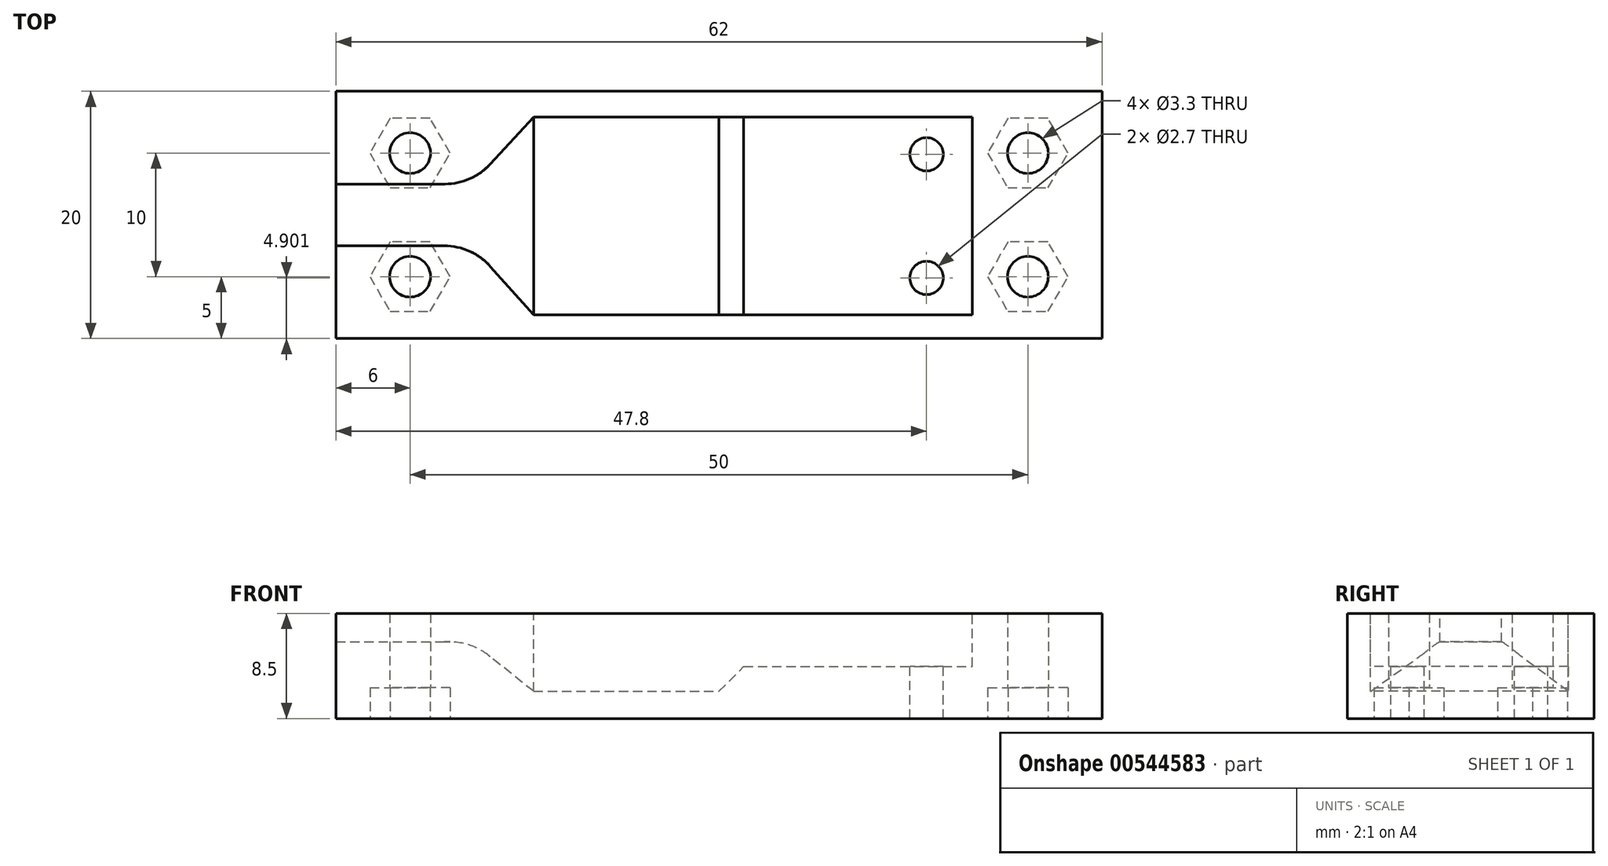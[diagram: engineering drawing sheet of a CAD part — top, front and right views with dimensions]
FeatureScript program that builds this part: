
annotation { "Feature Type Name" : "Feature", "Feature Type Description" : "" }
export const myFeature = defineFeature(function(context is Context, id is Id, definition is map)
    precondition{}
    {
        {
            var Q0;
            Q0=qCreatedBy(makeId("Top.planeOp"),FACE);
            var sketch = newSketch(context, id + "F0", { "sketchPlane" : qUnion([Q0])});
            skLineSegment(sketch, "E0.bottom", {"start": v(0, 0) * mm, "end": v(65, 0) * mm});
            skLineSegment(sketch, "E0.top", {"start": v(0, 20) * mm, "end": v(65, 20) * mm});
            skLineSegment(sketch, "E0.left", {"start": v(0, 0) * mm, "end": v(0, 20) * mm});
            skLineSegment(sketch, "E0.right", {"start": v(65, 0) * mm, "end": v(65, 20) * mm});
            skSolve(sketch);
        }
        {
            var Q0;
            Q0 = qSketchRegion(id + "F0", true);
            extrude(context, id + "F1", {"entities" : qUnion([Q0]), "depth" : 7.5 * mm, "offsetDistance" : 25 * mm});
        }
        {
            var Q0;
            Q0=makeQuery(id+"F1.opExtrude","CAP_FACE",FACE,{"disambiguationData":[OSD([sQuery(id+"F0.wireOp",EDGE,"E0.bottom"),sQuery(id+"F0.wireOp",EDGE,"E0.top"),sQuery(id+"F0.wireOp",EDGE,"E0.left"),sQuery(id+"F0.wireOp",EDGE,"E0.right")])],"isStart":true});
            var sketch = newSketch(context, id + "F2", { "sketchPlane" : qUnion([Q0])});
            skCircle(sketch, "E1.cCircle", {"center": v(6, -5) * mm, "radius": 2.81 * mm, "construction": true});
            skLineSegment(sketch, "E1.0", {"start": v(7.63, -7.81) * mm, "end": v(4.38, -7.81) * mm});
            skLineSegment(sketch, "E1.1", {"start": v(4.38, -7.81) * mm, "end": v(2.75, -5) * mm});
            skLineSegment(sketch, "E1.2", {"start": v(2.75, -5) * mm, "end": v(4.37, -2.19) * mm});
            skLineSegment(sketch, "E1.3", {"start": v(4.37, -2.19) * mm, "end": v(7.63, -2.19) * mm});
            skLineSegment(sketch, "E1.4", {"start": v(7.63, -2.19) * mm, "end": v(9.25, -5) * mm});
            skLineSegment(sketch, "E1.5", {"start": v(9.25, -5) * mm, "end": v(7.63, -7.81) * mm});
            skPoint(sketch, "E1.0.midPoint", {"position": v(6, -7.81) * mm});
            skCircle(sketch, "E2.cCircle", {"center": v(6, -15) * mm, "radius": 2.81 * mm, "construction": true});
            skLineSegment(sketch, "E2.0", {"start": v(4.38, -12.19) * mm, "end": v(7.63, -12.19) * mm});
            skLineSegment(sketch, "E2.1", {"start": v(7.63, -12.19) * mm, "end": v(9.25, -15) * mm});
            skLineSegment(sketch, "E2.2", {"start": v(9.25, -15) * mm, "end": v(7.63, -17.81) * mm});
            skLineSegment(sketch, "E2.3", {"start": v(7.62, -17.81) * mm, "end": v(4.38, -17.81) * mm});
            skLineSegment(sketch, "E2.4", {"start": v(4.38, -17.81) * mm, "end": v(2.75, -15) * mm});
            skLineSegment(sketch, "E2.5", {"start": v(2.75, -15) * mm, "end": v(4.38, -12.19) * mm});
            skPoint(sketch, "E2.0.midPoint", {"position": v(6, -12.19) * mm});
            skCircle(sketch, "E3.cCircle", {"center": v(56, -5) * mm, "radius": 2.81 * mm, "construction": true});
            skLineSegment(sketch, "E3.0", {"start": v(57.62, -7.81) * mm, "end": v(54.38, -7.81) * mm});
            skLineSegment(sketch, "E3.1", {"start": v(54.38, -7.81) * mm, "end": v(52.75, -5) * mm});
            skLineSegment(sketch, "E3.2", {"start": v(52.75, -5) * mm, "end": v(54.38, -2.19) * mm});
            skLineSegment(sketch, "E3.3", {"start": v(54.38, -2.19) * mm, "end": v(57.63, -2.19) * mm});
            skLineSegment(sketch, "E3.4", {"start": v(57.63, -2.19) * mm, "end": v(59.25, -5) * mm});
            skLineSegment(sketch, "E3.5", {"start": v(59.25, -5) * mm, "end": v(57.63, -7.81) * mm});
            skPoint(sketch, "E3.0.midPoint", {"position": v(56, -7.81) * mm});
            skCircle(sketch, "E4.cCircle", {"center": v(56, -15) * mm, "radius": 2.81 * mm, "construction": true});
            skLineSegment(sketch, "E4.0", {"start": v(57.62, -17.81) * mm, "end": v(54.37, -17.81) * mm});
            skLineSegment(sketch, "E4.1", {"start": v(54.37, -17.81) * mm, "end": v(52.75, -15) * mm});
            skLineSegment(sketch, "E4.2", {"start": v(52.75, -15) * mm, "end": v(54.38, -12.19) * mm});
            skLineSegment(sketch, "E4.3", {"start": v(54.38, -12.19) * mm, "end": v(57.63, -12.19) * mm});
            skLineSegment(sketch, "E4.4", {"start": v(57.63, -12.19) * mm, "end": v(59.25, -15) * mm});
            skLineSegment(sketch, "E4.5", {"start": v(59.25, -15) * mm, "end": v(57.62, -17.81) * mm});
            skPoint(sketch, "E4.0.midPoint", {"position": v(56, -17.81) * mm});
            skSolve(sketch);
        }
        {
            var Q0;
            Q0 = qSketchRegion(id + "F2", true);
            extrude(context, id + "F3", {"entities" : qUnion([Q0]), "operationType" : NewBodyOperationType.REMOVE, "oppositeDirection" : true, "depth" : 2.5 * mm, "offsetDistance" : 25 * mm});
        }
        {
            var Q0;
            Q0=makeQuery(id+"F3.boolean.opBoolean","COPY",FACE,{"derivedFrom":makeQuery(id+"F3.opExtrude","CAP_FACE",FACE,{"disambiguationData":[OSD([sQuery(id+"F2.wireOp",EDGE,"E1.0"),sQuery(id+"F2.wireOp",EDGE,"E1.1"),sQuery(id+"F2.wireOp",EDGE,"E1.2"),sQuery(id+"F2.wireOp",EDGE,"E1.3"),sQuery(id+"F2.wireOp",EDGE,"E1.4"),sQuery(id+"F2.wireOp",EDGE,"E1.5")])],"isStart":false})});
            var sketch = newSketch(context, id + "F4", { "sketchPlane" : qUnion([Q0])});
            skCircle(sketch, "E5", {"center": v(6, -5) * mm, "radius": 1.65 * mm});
            skCircle(sketch, "E6", {"center": v(6, -15) * mm, "radius": 1.65 * mm});
            skCircle(sketch, "E7", {"center": v(56, -5) * mm, "radius": 1.65 * mm});
            skCircle(sketch, "E8", {"center": v(56, -15) * mm, "radius": 1.65 * mm});
            skSolve(sketch);
        }
        {
            var Q0;
            Q0 = qSketchRegion(id + "F4", true);
            extrude(context, id + "F5", {"entities" : qUnion([Q0]), "operationType" : NewBodyOperationType.REMOVE, "oppositeDirection" : true, "depth" : 5 * mm, "offsetDistance" : 25 * mm});
        }
        {
            var Q0;
            Q0=makeQuery(id+"F1.opExtrude","CAP_FACE",FACE,{"disambiguationData":[OSD([sQuery(id+"F0.wireOp",EDGE,"E0.bottom"),sQuery(id+"F0.wireOp",EDGE,"E0.top"),sQuery(id+"F0.wireOp",EDGE,"E0.left"),sQuery(id+"F0.wireOp",EDGE,"E0.right")])],"isStart":false});
            var sketch = newSketch(context, id + "F6", { "sketchPlane" : qUnion([Q0])});
            skLineSegment(sketch, "E9.bottom", {"start": v(16, 17.9) * mm, "end": v(51, 17.9) * mm});
            skLineSegment(sketch, "E9.top", {"start": v(16, 1.9) * mm, "end": v(51, 1.9) * mm});
            skLineSegment(sketch, "E9.left", {"start": v(16, 17.9) * mm, "end": v(16, 1.9) * mm});
            skLineSegment(sketch, "E9.right", {"start": v(51, 17.9) * mm, "end": v(51, 1.9) * mm});
            skLineSegment(sketch, "E10.bottom", {"start": v(0, 12.5) * mm, "end": v(16, 12.5) * mm});
            skLineSegment(sketch, "E10.top", {"start": v(0, 7.5) * mm, "end": v(16, 7.5) * mm});
            skLineSegment(sketch, "E10.left", {"start": v(0, 12.5) * mm, "end": v(0, 7.5) * mm});
            skLineSegment(sketch, "E10.right", {"start": v(16, 12.5) * mm, "end": v(16, 7.5) * mm});
            skLineSegment(sketch, "E11", {"start": v(16, 17.9) * mm, "end": v(11, 12.5) * mm});
            skLineSegment(sketch, "E12", {"start": v(16, 1.9) * mm, "end": v(11, 7.5) * mm});
            skSolve(sketch);
        }
        {
            var Q0;
            Q0 = qSketchRegion(id + "F6", true);
            extrude(context, id + "F7", {"entities" : qUnion([Q0]), "operationType" : NewBodyOperationType.REMOVE, "oppositeDirection" : true, "depth" : 3.3 * mm, "offsetDistance" : 25 * mm});
        }
        {
            var Q0;
            Q0=makeQuery(id+"F7.boolean.opBoolean","COPY",FACE,{"derivedFrom":makeQuery(id+"F7.opExtrude","CAP_FACE",FACE,{"disambiguationData":[OSD([sQuery(id+"F6.wireOp",EDGE,"E9.bottom"),sQuery(id+"F6.wireOp",EDGE,"E9.top"),sQuery(id+"F6.wireOp",EDGE,"E9.right"),sQuery(id+"F6.wireOp",EDGE,"E10.bottom"),sQuery(id+"F6.wireOp",EDGE,"E10.top"),sQuery(id+"F6.wireOp",EDGE,"E10.left"),sQuery(id+"F6.wireOp",EDGE,"E11"),sQuery(id+"F6.wireOp",EDGE,"E12")])],"isStart":false})});
            var sketch = newSketch(context, id + "F8", { "sketchPlane" : qUnion([Q0])});
            skLineSegment(sketch, "E13.bottom", {"start": v(16, 17.9) * mm, "end": v(28, 17.9) * mm});
            skLineSegment(sketch, "E13.top", {"start": v(16, 1.9) * mm, "end": v(28, 1.9) * mm});
            skLineSegment(sketch, "E13.left", {"start": v(16, 17.9) * mm, "end": v(16, 1.9) * mm});
            skLineSegment(sketch, "E13.right", {"start": v(28, 17.9) * mm, "end": v(28, 1.9) * mm});
            skSolve(sketch);
        }
        {
            var Q0;
            Q0 = qSketchRegion(id + "F8", true);
            extrude(context, id + "F9", {"entities" : qUnion([Q0]), "operationType" : NewBodyOperationType.REMOVE, "oppositeDirection" : true, "depth" : 2 * mm, "offsetDistance" : 25 * mm});
        }
        {
            var Q0;
            {var subQ0=sQuery(id+"F6.wireOp",EDGE,"E9.right");var subQ1=sQuery(id+"F6.wireOp",EDGE,"E9.top");var subQ2=sQuery(id+"F6.wireOp",EDGE,"E9.bottom");Q0=makeQuery(id+"F9.boolean.opBoolean","SPLIT",FACE,{"disambiguationData":[TD([makeQuery(id+"F7.boolean.opBoolean","COPY",FACE,{"derivedFrom":makeQuery(id+"F7.opExtrude","SWEPT_FACE",FACE,{"disambiguationData":[OSD([subQ0])]})})])],"derivedFrom":makeQuery(id+"F7.boolean.opBoolean","COPY",FACE,{"derivedFrom":makeQuery(id+"F7.opExtrude","CAP_FACE",FACE,{"disambiguationData":[OSD([subQ2,subQ1,subQ0,sQuery(id+"F6.wireOp",EDGE,"E10.bottom"),sQuery(id+"F6.wireOp",EDGE,"E10.top"),sQuery(id+"F6.wireOp",EDGE,"E10.left"),sQuery(id+"F6.wireOp",EDGE,"E11"),sQuery(id+"F6.wireOp",EDGE,"E12")])],"isStart":false})})});}
            var sketch = newSketch(context, id + "F10", { "sketchPlane" : qUnion([Q0])});
            skCircle(sketch, "E14", {"center": v(47.8, 14.9) * mm, "radius": 1.35 * mm});
            skCircle(sketch, "E15", {"center": v(47.8, 4.9) * mm, "radius": 1.35 * mm});
            skSolve(sketch);
        }
        {
            var Q0;
            Q0 = qSketchRegion(id + "F10", true);
            extrude(context, id + "F11", {"entities" : qUnion([Q0]), "operationType" : NewBodyOperationType.REMOVE, "oppositeDirection" : true, "depth" : 5 * mm, "offsetDistance" : 25 * mm});
        }
        {
            var Q0;
            Q0=makeQuery(id+"F9.boolean.opBoolean","COPY",EDGE,{"derivedFrom":makeQuery(id+"F9.opExtrude","CAP_EDGE",EDGE,{"disambiguationData":[OSD([sQuery(id+"F8.wireOp",EDGE,"E13.right")])],"isStart":true})});
            chamfer(context, id + "F12", {"entities" : qUnion([Q0]), "width" : 5 * mm, "tangentPropagation" : true});
        }
        {
            var Q0;
            Q0=makeQuery(id+"F1.opExtrude","SWEPT_FACE",FACE,{"disambiguationData":[OSD([sQuery(id+"F0.wireOp",EDGE,"E0.bottom")])]});
            var sketch = newSketch(context, id + "F13", { "sketchPlane" : qUnion([Q0])});
            skLineSegment(sketch, "E16", {"start": v(16, 2.2) * mm, "end": v(11, 2.2) * mm});
            skLineSegment(sketch, "E17", {"start": v(11, 2.2) * mm, "end": v(11, 6.2) * mm});
            skLineSegment(sketch, "E18", {"start": v(11, 6.2) * mm, "end": v(16, 2.2) * mm});
            skSolve(sketch);
        }
        {
            var Q0;
            {var subQ0=sQuery(id+"F6.wireOp",EDGE,"E10.bottom");var subQ1=sQuery(id+"F6.wireOp",EDGE,"E9.bottom");var subQ2=sQuery(id+"F6.wireOp",EDGE,"E9.top");var subQ3=sQuery(id+"F6.wireOp",EDGE,"E10.top");var subQ4=sQuery(id+"F6.wireOp",EDGE,"E11");var subQ5=sQuery(id+"F6.wireOp",EDGE,"E12");Q0=makeQuery(id+"F9.boolean.opBoolean","SPLIT",FACE,{"disambiguationData":[TD([makeQuery(id+"F1.opExtrude","SWEPT_FACE",FACE,{"disambiguationData":[OSD([sQuery(id+"F0.wireOp",EDGE,"E0.left")])]})])],"derivedFrom":makeQuery(id+"F7.boolean.opBoolean","COPY",FACE,{"derivedFrom":makeQuery(id+"F7.opExtrude","CAP_FACE",FACE,{"disambiguationData":[OSD([subQ1,subQ2,sQuery(id+"F6.wireOp",EDGE,"E9.right"),subQ0,subQ3,sQuery(id+"F6.wireOp",EDGE,"E10.left"),subQ4,subQ5])],"isStart":false})})});}
            var sketch = newSketch(context, id + "F14", { "sketchPlane" : qUnion([Q0])});
            skLineSegment(sketch, "E19", {"start": v(11, 12.5) * mm, "end": v(11, 7.5) * mm});
            skLineSegment(sketch, "E20", {"start": v(11, 7.5) * mm, "end": v(16, 1.9) * mm});
            skLineSegment(sketch, "E21", {"start": v(16, 1.9) * mm, "end": v(16, 17.9) * mm});
            skLineSegment(sketch, "E22", {"start": v(16, 17.9) * mm, "end": v(11, 12.5) * mm});
            skSolve(sketch);
        }
        {
            var Q0;
            Q0 = qSketchRegion(id + "F14", true);
            extrude(context, id + "F15", {"entities" : qUnion([Q0]), "operationType" : NewBodyOperationType.REMOVE, "oppositeDirection" : true, "depth" : 2 * mm, "offsetDistance" : 25 * mm});
        }
        {
            var Q0;
            Q0 = qSketchRegion(id + "F13", true);
            extrude(context, id + "F16", {"entities" : qUnion([Q0]), "operationType" : NewBodyOperationType.ADD, "oppositeDirection" : true, "depth" : 20 * mm, "offsetDistance" : 25 * mm});
        }
        {
            var Q0;
            Q0=makeQuery(id+"F1.opExtrude","SWEPT_FACE",FACE,{"disambiguationData":[OSD([sQuery(id+"F0.wireOp",EDGE,"E0.right")])]});
            var sketch = newSketch(context, id + "F17", { "sketchPlane" : qUnion([Q0])});
            skLineSegment(sketch, "E23.bottom", {"start": v(0, 7.5) * mm, "end": v(20, 7.5) * mm});
            skLineSegment(sketch, "E23.top", {"start": v(0, 0) * mm, "end": v(20, 0) * mm});
            skLineSegment(sketch, "E23.left", {"start": v(0, 7.5) * mm, "end": v(0, 0) * mm});
            skLineSegment(sketch, "E23.right", {"start": v(20, 7.5) * mm, "end": v(20, 0) * mm});
            skSolve(sketch);
        }
        {
            var Q0;
            Q0 = qSketchRegion(id + "F17", true);
            extrude(context, id + "F18", {"entities" : qUnion([Q0]), "operationType" : NewBodyOperationType.REMOVE, "oppositeDirection" : true, "depth" : 3 * mm, "offsetDistance" : 25 * mm});
        }
        {
            var Q0;
            {var subQ0=sQuery(id+"F6.wireOp",EDGE,"E10.bottom");var subQ1=sQuery(id+"F6.wireOp",EDGE,"E9.bottom");var subQ2=sQuery(id+"F6.wireOp",EDGE,"E9.top");var subQ3=sQuery(id+"F6.wireOp",EDGE,"E10.top");var subQ4=sQuery(id+"F6.wireOp",EDGE,"E11");var subQ5=sQuery(id+"F6.wireOp",EDGE,"E12");Q0=makeQuery(id+"F9.boolean.opBoolean","SPLIT",FACE,{"disambiguationData":[TD([makeQuery(id+"F1.opExtrude","SWEPT_FACE",FACE,{"disambiguationData":[OSD([sQuery(id+"F0.wireOp",EDGE,"E0.left")])]})])],"derivedFrom":makeQuery(id+"F7.boolean.opBoolean","COPY",FACE,{"derivedFrom":makeQuery(id+"F7.opExtrude","CAP_FACE",FACE,{"disambiguationData":[OSD([subQ1,subQ2,sQuery(id+"F6.wireOp",EDGE,"E9.right"),subQ0,subQ3,sQuery(id+"F6.wireOp",EDGE,"E10.left"),subQ4,subQ5])],"isStart":false})})});}
            var sketch = newSketch(context, id + "F19", { "sketchPlane" : qUnion([Q0])});
            skLineSegment(sketch, "E24.bottom", {"start": v(0, 7.5) * mm, "end": v(11, 7.5) * mm});
            skLineSegment(sketch, "E24.top", {"start": v(0, 12.5) * mm, "end": v(11, 12.5) * mm});
            skLineSegment(sketch, "E24.left", {"start": v(0, 7.5) * mm, "end": v(0, 12.5) * mm});
            skLineSegment(sketch, "E24.right", {"start": v(11, 7.5) * mm, "end": v(11, 12.5) * mm});
            skSolve(sketch);
        }
        {
            var Q0;
            Q0 = qSketchRegion(id + "F19", true);
            extrude(context, id + "F20", {"entities" : qUnion([Q0]), "operationType" : NewBodyOperationType.ADD, "depth" : 2 * mm, "offsetDistance" : 25 * mm});
        }
        {
            var Q0;
            Q0=makeQuery(id+"F1.opExtrude","CAP_FACE",FACE,{"disambiguationData":[OSD([sQuery(id+"F0.wireOp",EDGE,"E0.bottom"),sQuery(id+"F0.wireOp",EDGE,"E0.top"),sQuery(id+"F0.wireOp",EDGE,"E0.left"),sQuery(id+"F0.wireOp",EDGE,"E0.right")])],"isStart":false});
            extrude(context, id + "F21", {"entities" : qUnion([Q0]), "operationType" : NewBodyOperationType.ADD, "depth" : 1 * mm, "offsetDistance" : 25 * mm});
        }
        {
            var Q0;
            {var subQ0=sQuery(id+"F6.wireOp",EDGE,"E11");var subQ1=sQuery(id+"F6.wireOp",EDGE,"E10.bottom");Q0=makeQuery(id+"F21.boolean.opBoolean","MERGE",EDGE,{"derivedFrom":[makeQuery(id+"F7.boolean.opBoolean","COPY",EDGE,{"derivedFrom":makeQuery(id+"F7.opExtrude","SWEPT_EDGE",EDGE,{"disambiguationData":[OSD([subQ1,subQ0])]})}),makeQuery(id+"F21.opExtrude","SWEPT_EDGE",EDGE,{"disambiguationData":[OSD([subQ1,subQ0])]})]});}
            var Q1;
            Q1=makeQuery(id+"F20.boolean.opBoolean","MERGE",EDGE,{"derivedFrom":[makeQuery(id+"F16.opExtrude","SWEPT_EDGE",EDGE,{"disambiguationData":[OSD([sQuery(id+"F13.wireOp",EDGE,"E17"),sQuery(id+"F13.wireOp",EDGE,"E18")])]}),makeQuery(id+"F20.opExtrude","CAP_EDGE",EDGE,{"disambiguationData":[OSD([sQuery(id+"F19.wireOp",EDGE,"E24.right")])],"isStart":false})]});
            var Q2;
            {var subQ0=sQuery(id+"F6.wireOp",EDGE,"E12");var subQ1=sQuery(id+"F6.wireOp",EDGE,"E10.top");Q2=makeQuery(id+"F21.boolean.opBoolean","MERGE",EDGE,{"derivedFrom":[makeQuery(id+"F7.boolean.opBoolean","COPY",EDGE,{"derivedFrom":makeQuery(id+"F7.opExtrude","SWEPT_EDGE",EDGE,{"disambiguationData":[OSD([subQ1,subQ0])]})}),makeQuery(id+"F21.opExtrude","SWEPT_EDGE",EDGE,{"disambiguationData":[OSD([subQ1,subQ0])]})]});}
            fillet(context, id + "F22", {"entities" : qUnion([Q0, Q1, Q2]), "radius" : 5 * mm, "tangentPropagation" : true, "allowEdgeOverflow" : false});
        }
        {
            var Q0;
            {var subQ0=sQuery(id+"F6.wireOp",EDGE,"E9.right");Q0=makeQuery(id+"F21.boolean.opBoolean","MERGE",FACE,{"derivedFrom":[makeQuery(id+"F7.boolean.opBoolean","COPY",FACE,{"derivedFrom":makeQuery(id+"F7.opExtrude","SWEPT_FACE",FACE,{"disambiguationData":[OSD([subQ0])]})}),makeQuery(id+"F21.opExtrude","SWEPT_FACE",FACE,{"disambiguationData":[OSD([subQ0])]})]});}
            extrude(context, id + "F23", {"entities" : qUnion([Q0]), "operationType" : NewBodyOperationType.REMOVE, "oppositeDirection" : true, "depth" : 0.5 * mm, "offsetDistance" : 25 * mm});
        }
    });
